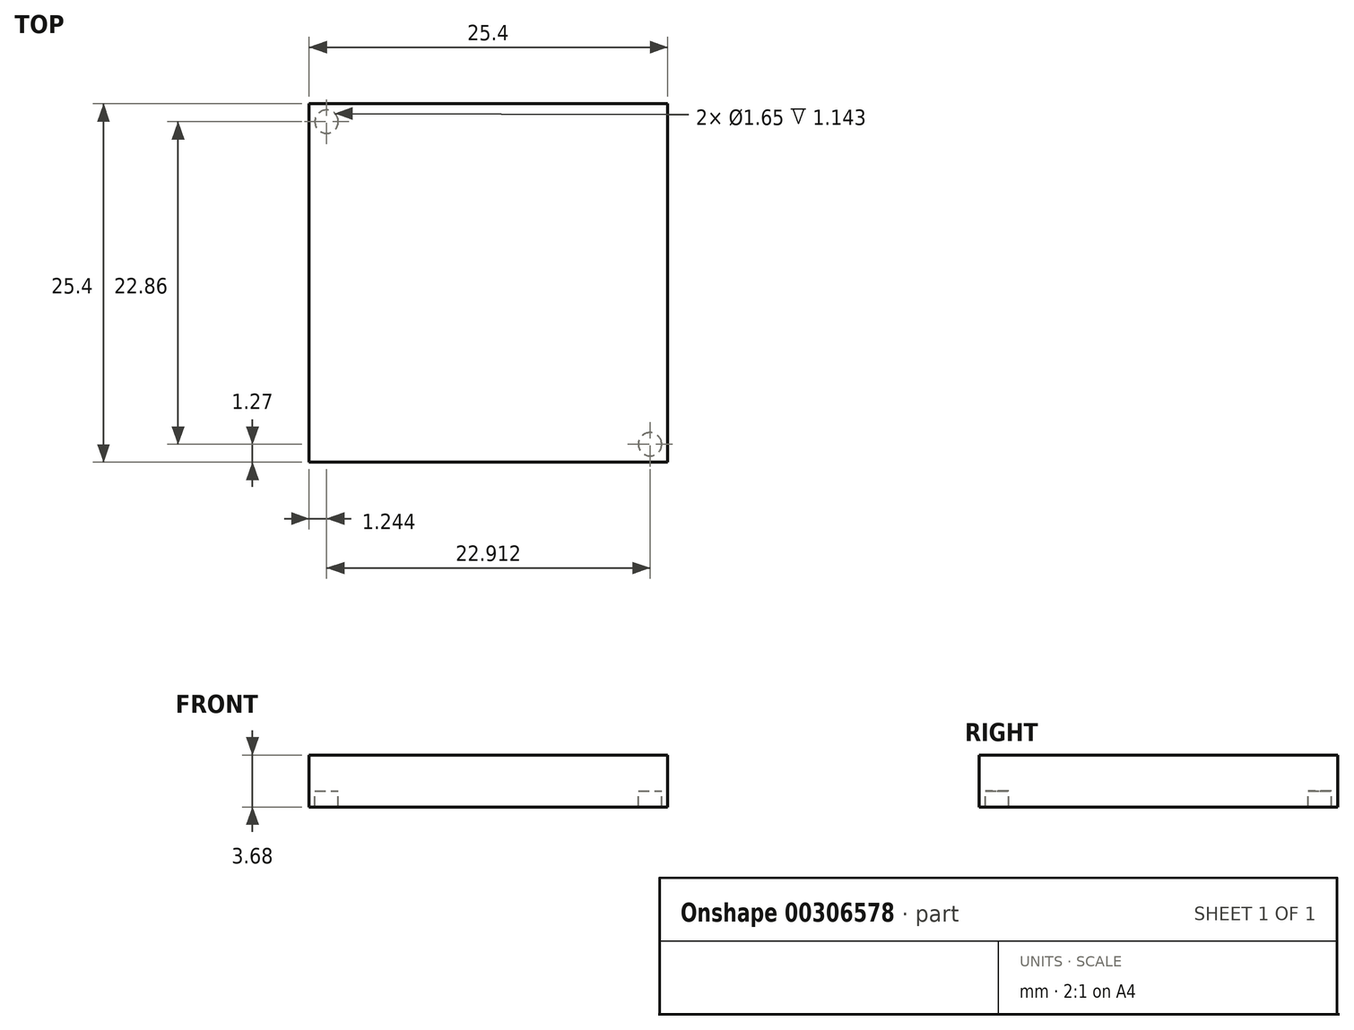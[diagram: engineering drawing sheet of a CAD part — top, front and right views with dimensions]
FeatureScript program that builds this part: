
annotation { "Feature Type Name" : "Feature", "Feature Type Description" : "" }
export const myFeature = defineFeature(function(context is Context, id is Id, definition is map)
    precondition{}
    {
        {
            var Q0;
            Q0=qCreatedBy(makeId("Top.planeOp"),FACE);
            var sketch = newSketch(context, id + "F0", { "sketchPlane" : qUnion([Q0])});
            skLineSegment(sketch, "E0", {"start": v(-12.7, 12.7) * mm, "end": v(-12.7, -12.7) * mm});
            skLineSegment(sketch, "E1.MirrorCS", {"start": v(12.7, 12.7) * mm, "end": v(12.7, -12.7) * mm});
            skLineSegment(sketch, "E2", {"start": v(-12.7, -12.7) * mm, "end": v(12.7, -12.7) * mm});
            skLineSegment(sketch, "E3", {"start": v(-12.7, 12.7) * mm, "end": v(12.7, 12.7) * mm});
            skSolve(sketch);
        }
        {
            var Q0;
            Q0=makeQuery(id+"F0.imprint","IMPRINT",FACE,{"disambiguationData":[TD([[makeQuery(id+"F0.imprint","IMPRINT",EDGE,{"derivedFrom":sQuery(id+"F0.wireOp",EDGE,"E0")}),1.0]])]});
            extrude(context, id + "F1", {"entities" : qUnion([Q0]), "endBound" : BoundingType.SYMMETRIC, "depth" : 2.54 * mm});
        }
        {
            var Q0;
            Q0=makeQuery(id+"F1.opExtrude","CAP_FACE",FACE,{"disambiguationData":[OSD([sQuery(id+"F0.wireOp",EDGE,"E0"),sQuery(id+"F0.wireOp",EDGE,"E1.MirrorCS"),sQuery(id+"F0.wireOp",EDGE,"E2"),sQuery(id+"F0.wireOp",EDGE,"E3")])],"isStart":true});
            var sketch = newSketch(context, id + "F2", { "sketchPlane" : qUnion([Q0])});
            skPoint(sketch, "E4.endSnap0", {"position": v(0, -12.7) * mm});
            skCircle(sketch, "E5", {"center": v(-11.46, 11.43) * mm, "radius": 0.83 * mm});
            skCircle(sketch, "E6.MirrorC", {"center": v(-11.46, -11.43) * mm, "radius": 0.83 * mm});
            skCircle(sketch, "E7.MirrorC", {"center": v(11.46, 11.43) * mm, "radius": 0.83 * mm});
            skCircle(sketch, "E8.MirrorC", {"center": v(11.46, -11.43) * mm, "radius": 0.83 * mm});
            skSolve(sketch);
        }
        {
            var Q0;
            Q0=makeQuery(id+"F2.imprint","IMPRINT",FACE,{"disambiguationData":[TD([[makeQuery(id+"F2.imprint","IMPRINT",EDGE,{"derivedFrom":sQuery(id+"F2.wireOp",EDGE,"E5")}),1.0]])]});
            var Q1;
            Q1=makeQuery(id+"F2.imprint","IMPRINT",FACE,{"disambiguationData":[TD([[makeQuery(id+"F2.imprint","IMPRINT",EDGE,{"derivedFrom":sQuery(id+"F2.wireOp",EDGE,"E7.MirrorC")}),-1.0]])]});
            var Q2;
            Q2=makeQuery(id+"F2.imprint","IMPRINT",FACE,{"disambiguationData":[TD([[makeQuery(id+"F2.imprint","IMPRINT",EDGE,{"derivedFrom":sQuery(id+"F2.wireOp",EDGE,"E8.MirrorC")}),1.0]])]});
            var Q3;
            Q3=makeQuery(id+"F2.imprint","IMPRINT",FACE,{"disambiguationData":[TD([[makeQuery(id+"F2.imprint","IMPRINT",EDGE,{"derivedFrom":sQuery(id+"F2.wireOp",EDGE,"E6.MirrorC")}),-1.0]])]});
            extrude(context, id + "F3", {"entities" : qUnion([Q0, Q1, Q2, Q3]), "operationType" : NewBodyOperationType.ADD, "depth" : 1.14 * mm});
        }
    });
